# Revit family: НЕВАТОМ_Крышный переход KP для VKR, версия 1
name_source: partatom
category: Арматура воздуховодов
revit_build: Autodesk Revit 2017 (Build: 20170118_1100(x64)
units: mm (PartAtom-declared; Revit-internal decimal feet)

## family parameters
Всегда вертикально = Нет
На основе рабочей плоскости = Нет
Общий = Нет
При загрузке вырезать с полостями = Нет
Размер круглого соединителя = Использовать диаметр
Тип детали = Вставляется

## types (5) — shared parameters
ADSK_Единица измерения = шт.
ADSK_Завод-изготовитель = НЕВАТОМ
ADSK_Количество = 1
ADSK_Наименование = Крышный переход
ADSK_Потеря давления воздуха = 0.0 Па
ADSK_Размер_Высота = 470 мм
ADSK_Расход воздуха = 0.0 л/с
Nevatom_URL = https://t.me
d отв = 11 мм

## per-type parameters (varying)
| type | ADSK_Марка | ADSK_Размер_Длина | ADSK_Размер_Ширина | B | C | D | А | Материал |
| КР 30 | KP 30 | 616 мм | 616 мм | 246 мм | 270 мм | 616 мм | 296 мм | Оцинкованная сталь |
| КР 40 | KP 40 | 716 мм | 716 мм | 346 мм | 370 мм | 716 мм | 396 мм | <По категории> |
| КР 56 | KP 56 | 876 мм | 876 мм | 506 мм | 530 мм | 876 мм | 556 мм | <По категории> |
| КР 63 | KP 63 | 946 мм | 946 мм | 576 мм | 600 мм | 946 мм | 626 мм | <По категории> |
| КР 90 | KP 90 | 1216 мм | 1216 мм | 846 мм | 870 мм | 1216 мм | 896 мм | Оцинкованная сталь |
